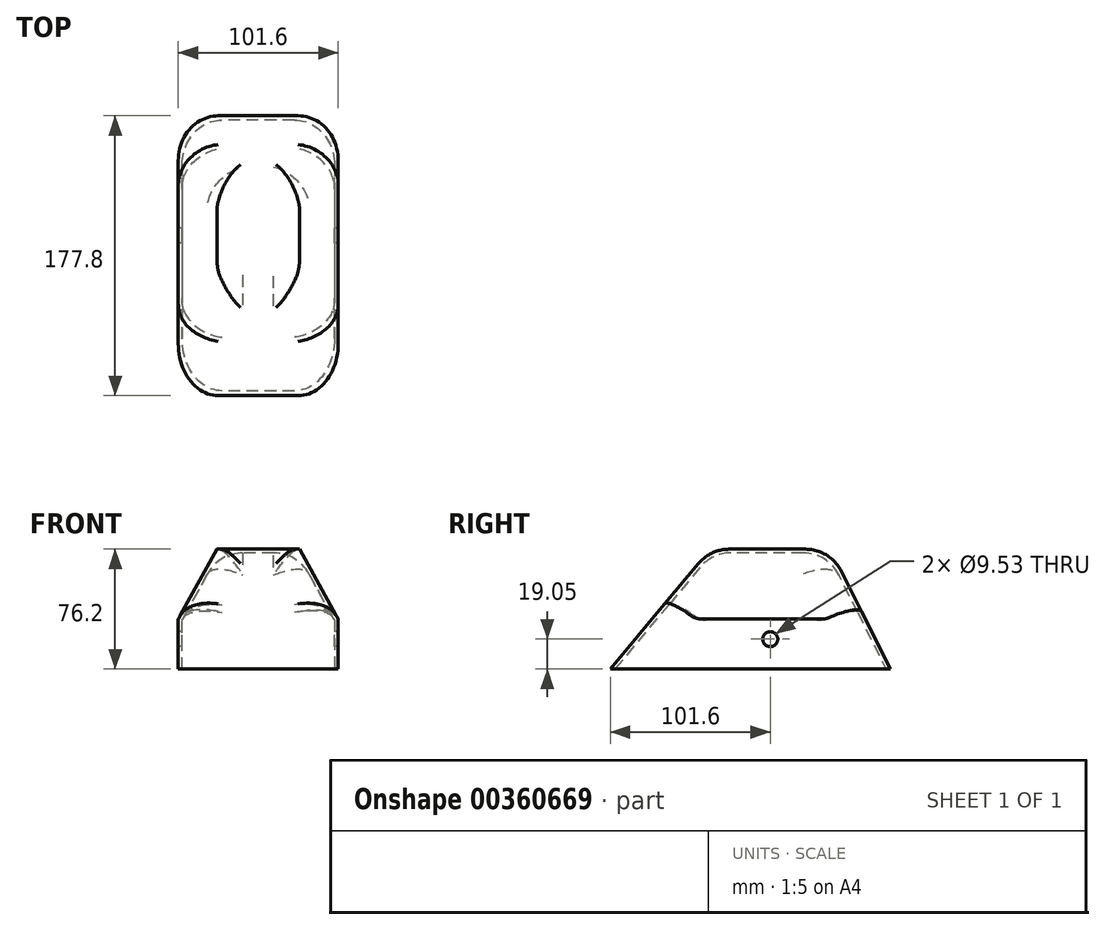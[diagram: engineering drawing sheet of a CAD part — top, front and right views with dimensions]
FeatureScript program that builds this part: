
annotation { "Feature Type Name" : "Feature", "Feature Type Description" : "" }
export const myFeature = defineFeature(function(context is Context, id is Id, definition is map)
    precondition{}
    {
        {
            var Q0;
            Q0=qCreatedBy(makeId("Right.planeOp"),FACE);
            var sketch = newSketch(context, id + "F0", { "sketchPlane" : qUnion([Q0])});
            skLineSegment(sketch, "E0", {"start": v(0, 0) * mm, "end": v(-101.6, 0) * mm});
            skLineSegment(sketch, "E1", {"start": v(-101.6, 0) * mm, "end": v(-38.1, 76.2) * mm});
            skLineSegment(sketch, "E2", {"start": v(-38.1, 76.2) * mm, "end": v(38.1, 76.2) * mm});
            skLineSegment(sketch, "E3", {"start": v(38.1, 76.2) * mm, "end": v(76.2, 0) * mm});
            skLineSegment(sketch, "E4", {"start": v(76.2, 0) * mm, "end": v(0, 0) * mm});
            skLineSegment(sketch, "E5", {"start": v(-38.1, 76.2) * mm, "end": v(0, 0) * mm, "construction": true});
            skLineSegment(sketch, "E6", {"start": v(38.1, 76.2) * mm, "end": v(0, 0) * mm, "construction": true});
            skSolve(sketch);
        }
        {
            var Q0;
            {var subQ1=sQuery(id+"F0.wireOp",EDGE,"E1");Q0=makeQuery(id+"F0.imprint","IMPRINT",FACE,{"disambiguationData":[TD([[makeQuery(id+"F0.imprint","IMPRINT",EDGE,{"derivedFrom":subQ1}),-1.0]])]});}
            extrude(context, id + "F1", {"entities" : qUnion([Q0]), "depth" : 101.6 * mm});
        }
        {
            var Q0;
            Q0=qCreatedBy(makeId("Right.planeOp"),FACE);
            var sketch = newSketch(context, id + "F2", { "sketchPlane" : qUnion([Q0])});
            skCircle(sketch, "E7", {"center": v(0, 19.05) * mm, "radius": 4.76 * mm});
            skSolve(sketch);
        }
        {
            var Q0;
            Q0=qCreatedBy(makeId("Front.planeOp"),FACE);
            var sketch = newSketch(context, id + "F3", { "sketchPlane" : qUnion([Q0])});
            skLineSegment(sketch, "E8", {"start": v(0, 0) * mm, "end": v(0, 31.75) * mm});
            skLineSegment(sketch, "E9", {"start": v(0, 31.75) * mm, "end": v(24.6, 76.2) * mm});
            skLineSegment(sketch, "E10", {"start": v(24.6, 76.2) * mm, "end": v(77, 76.2) * mm});
            skLineSegment(sketch, "E11", {"start": v(77, 76.2) * mm, "end": v(101.6, 31.75) * mm});
            skLineSegment(sketch, "E12", {"start": v(101.6, 31.75) * mm, "end": v(145.44, 31.75) * mm});
            skLineSegment(sketch, "E13", {"start": v(145.44, 31.75) * mm, "end": v(145.44, 123.88) * mm});
            skLineSegment(sketch, "E14", {"start": v(145.44, 123.88) * mm, "end": v(-43.84, 123.88) * mm});
            skLineSegment(sketch, "E15", {"start": v(-43.84, 123.88) * mm, "end": v(-43.84, 31.75) * mm});
            skLineSegment(sketch, "E16", {"start": v(-43.84, 31.75) * mm, "end": v(0, 31.75) * mm});
            skSolve(sketch);
        }
        {
            var Q0;
            Q0=makeQuery(id+"F3.imprint","IMPRINT",FACE,{"disambiguationData":[TD([[makeQuery(id+"F3.imprint","IMPRINT",EDGE,{"derivedFrom":sQuery(id+"F3.wireOp",EDGE,"E9")}),1.0]])]});
            extrude(context, id + "F4", {"entities" : qUnion([Q0]), "operationType" : NewBodyOperationType.REMOVE, "endBound" : BoundingType.THROUGH_ALL, "oppositeDirection" : true, "depth" : 25.4 * mm, "hasSecondDirection" : true, "secondDirectionBound" : SecondDirectionBoundingType.THROUGH_ALL, "secondDirectionOppositeDirection" : false, "secondDirectionDepth" : 25.4 * mm});
        }
        {
            var Q0;
            Q0=makeQuery(id+"F1.opExtrude","SWEPT_FACE",FACE,{"disambiguationData":[OSD([sQuery(id+"F0.wireOp",EDGE,"E0"),sQuery(id+"F0.wireOp",EDGE,"E4")])]});
            shell(context, id + "F5", {"entities" : qUnion([Q0]), "thickness" : 2.38 * mm});
        }
        {
            var Q0;
            Q0=qSketchRegion(id+"F2",true);
            extrude(context, id + "F6", {"entities" : qUnion([Q0]), "operationType" : NewBodyOperationType.REMOVE, "endBound" : BoundingType.THROUGH_ALL, "depth" : 25.4 * mm});
        }
        {
            var Q0;
            {var subQ0=sQuery(id+"F0.wireOp",EDGE,"E3");Q0=makeQuery(id+"F5.opShell","OFFSET_EDGE",EDGE,{"disambiguationData":[OSD([subQ0]),TDD([makeQuery(id+"F1.opExtrude","CAP_EDGE",EDGE,{"disambiguationData":[OSD([subQ0])],"isStart":true})])]});}
            var Q1;
            Q1=makeQuery(id+"F5.opShell","OFFSET_EDGE",EDGE,{"disambiguationData":[OSD([sQuery(id+"F3.wireOp",EDGE,"E9"),sQuery(id+"F3.wireOp",EDGE,"E16")])]});
            var Q2;
            {var subQ0=sQuery(id+"F0.wireOp",EDGE,"E1");Q2=makeQuery(id+"F5.opShell","OFFSET_EDGE",EDGE,{"disambiguationData":[OSD([subQ0]),TDD([makeQuery(id+"F1.opExtrude","CAP_EDGE",EDGE,{"disambiguationData":[OSD([subQ0])],"isStart":true})])]});}
            var Q3;
            Q3=makeQuery(id+"F5.opShell","OFFSET_EDGE",EDGE,{"disambiguationData":[OSD([sQuery(id+"F3.wireOp",EDGE,"E9"),sQuery(id+"F3.wireOp",EDGE,"E10")])]});
            var Q4;
            Q4=makeQuery(id+"F5.opShell","OFFSET_EDGE",EDGE,{"disambiguationData":[OSD([sQuery(id+"F0.wireOp",EDGE,"E2"),sQuery(id+"F0.wireOp",EDGE,"E3")])]});
            var Q5;
            Q5=makeQuery(id+"F5.opShell","OFFSET_EDGE",EDGE,{"disambiguationData":[OSD([sQuery(id+"F0.wireOp",EDGE,"E1"),sQuery(id+"F0.wireOp",EDGE,"E2")])]});
            var Q6;
            Q6=makeQuery(id+"F5.opShell","OFFSET_EDGE",EDGE,{"disambiguationData":[OSD([sQuery(id+"F0.wireOp",EDGE,"E1"),sQuery(id+"F3.wireOp",EDGE,"E11")])]});
            var Q7;
            Q7=makeQuery(id+"F5.opShell","OFFSET_EDGE",EDGE,{"disambiguationData":[OSD([sQuery(id+"F0.wireOp",EDGE,"E3"),sQuery(id+"F3.wireOp",EDGE,"E11")])]});
            var Q8;
            Q8=makeQuery(id+"F5.opShell","OFFSET_EDGE",EDGE,{"disambiguationData":[OSD([sQuery(id+"F3.wireOp",EDGE,"E11"),sQuery(id+"F3.wireOp",EDGE,"E12")])]});
            var Q9;
            Q9=makeQuery(id+"F5.opShell","OFFSET_EDGE",EDGE,{"disambiguationData":[OSD([sQuery(id+"F0.wireOp",EDGE,"E1"),sQuery(id+"F3.wireOp",EDGE,"E9")])]});
            var Q10;
            {var subQ0=sQuery(id+"F0.wireOp",EDGE,"E1");Q10=makeQuery(id+"F5.opShell","OFFSET_EDGE",EDGE,{"disambiguationData":[OSD([subQ0]),TDD([makeQuery(id+"F1.opExtrude","CAP_EDGE",EDGE,{"disambiguationData":[OSD([subQ0])],"isStart":false})])]});}
            var Q11;
            {var subQ0=sQuery(id+"F0.wireOp",EDGE,"E3");Q11=makeQuery(id+"F5.opShell","OFFSET_EDGE",EDGE,{"disambiguationData":[OSD([subQ0]),TDD([makeQuery(id+"F1.opExtrude","CAP_EDGE",EDGE,{"disambiguationData":[OSD([subQ0])],"isStart":false})])]});}
            var Q12;
            Q12=makeQuery(id+"F5.opShell","OFFSET_EDGE",EDGE,{"disambiguationData":[OSD([sQuery(id+"F3.wireOp",EDGE,"E10"),sQuery(id+"F3.wireOp",EDGE,"E11")])]});
            var Q13;
            Q13=makeQuery(id+"F5.opShell","OFFSET_EDGE",EDGE,{"disambiguationData":[OSD([sQuery(id+"F0.wireOp",EDGE,"E3"),sQuery(id+"F3.wireOp",EDGE,"E9")])]});
            var Q14;
            Q14=makeQuery(id+"F1.opExtrude","CAP_EDGE",EDGE,{"disambiguationData":[OSD([sQuery(id+"F0.wireOp",EDGE,"E1")])],"isStart":true});
            var Q15;
            Q15=makeQuery(id+"F4.boolean.opBoolean","COPY",EDGE,{"derivedFrom":makeQuery(id+"F4.opExtrude","SWEPT_EDGE",EDGE,{"disambiguationData":[OSD([sQuery(id+"F3.wireOp",EDGE,"E9"),sQuery(id+"F3.wireOp",EDGE,"E16")])]})});
            var Q16;
            Q16=makeQuery(id+"F4.boolean.opBoolean","INTERSECT",EDGE,{"derivedFrom":[makeQuery(id+"F1.opExtrude","SWEPT_FACE",FACE,{"disambiguationData":[OSD([sQuery(id+"F0.wireOp",EDGE,"E1")])]}),makeQuery(id+"F4.opExtrude","SWEPT_FACE",FACE,{"disambiguationData":[OSD([sQuery(id+"F3.wireOp",EDGE,"E9")])]})]});
            var Q17;
            Q17=makeQuery(id+"F4.boolean.opBoolean","COPY",EDGE,{"derivedFrom":makeQuery(id+"F4.opExtrude","SWEPT_EDGE",EDGE,{"disambiguationData":[OSD([sQuery(id+"F3.wireOp",EDGE,"E9"),sQuery(id+"F3.wireOp",EDGE,"E10")])]})});
            var Q18;
            Q18=makeQuery(id+"F4.boolean.opBoolean","INTERSECT",EDGE,{"derivedFrom":[makeQuery(id+"F1.opExtrude","SWEPT_FACE",FACE,{"disambiguationData":[OSD([sQuery(id+"F0.wireOp",EDGE,"E3")])]}),makeQuery(id+"F4.opExtrude","SWEPT_FACE",FACE,{"disambiguationData":[OSD([sQuery(id+"F3.wireOp",EDGE,"E9")])]})]});
            var Q19;
            Q19=makeQuery(id+"F1.opExtrude","CAP_EDGE",EDGE,{"disambiguationData":[OSD([sQuery(id+"F0.wireOp",EDGE,"E3")])],"isStart":true});
            var Q20;
            Q20=makeQuery(id+"F1.opExtrude","SWEPT_EDGE",EDGE,{"disambiguationData":[OSD([sQuery(id+"F0.wireOp",EDGE,"E1"),sQuery(id+"F0.wireOp",EDGE,"E2")])]});
            var Q21;
            Q21=makeQuery(id+"F4.boolean.opBoolean","COPY",EDGE,{"derivedFrom":makeQuery(id+"F4.opExtrude","SWEPT_EDGE",EDGE,{"disambiguationData":[OSD([sQuery(id+"F3.wireOp",EDGE,"E10"),sQuery(id+"F3.wireOp",EDGE,"E11")])]})});
            var Q22;
            Q22=makeQuery(id+"F4.boolean.opBoolean","INTERSECT",EDGE,{"derivedFrom":[makeQuery(id+"F1.opExtrude","SWEPT_FACE",FACE,{"disambiguationData":[OSD([sQuery(id+"F0.wireOp",EDGE,"E1")])]}),makeQuery(id+"F4.opExtrude","SWEPT_FACE",FACE,{"disambiguationData":[OSD([sQuery(id+"F3.wireOp",EDGE,"E11")])]})]});
            var Q23;
            Q23=makeQuery(id+"F1.opExtrude","CAP_EDGE",EDGE,{"disambiguationData":[OSD([sQuery(id+"F0.wireOp",EDGE,"E1")])],"isStart":false});
            var Q24;
            Q24=makeQuery(id+"F4.boolean.opBoolean","COPY",EDGE,{"derivedFrom":makeQuery(id+"F4.opExtrude","SWEPT_EDGE",EDGE,{"disambiguationData":[OSD([sQuery(id+"F3.wireOp",EDGE,"E11"),sQuery(id+"F3.wireOp",EDGE,"E12")])]})});
            var Q25;
            Q25=makeQuery(id+"F1.opExtrude","CAP_EDGE",EDGE,{"disambiguationData":[OSD([sQuery(id+"F0.wireOp",EDGE,"E3")])],"isStart":false});
            var Q26;
            Q26=makeQuery(id+"F4.boolean.opBoolean","INTERSECT",EDGE,{"derivedFrom":[makeQuery(id+"F1.opExtrude","SWEPT_FACE",FACE,{"disambiguationData":[OSD([sQuery(id+"F0.wireOp",EDGE,"E3")])]}),makeQuery(id+"F4.opExtrude","SWEPT_FACE",FACE,{"disambiguationData":[OSD([sQuery(id+"F3.wireOp",EDGE,"E11")])]})]});
            var Q27;
            Q27=makeQuery(id+"F1.opExtrude","SWEPT_EDGE",EDGE,{"disambiguationData":[OSD([sQuery(id+"F0.wireOp",EDGE,"E2"),sQuery(id+"F0.wireOp",EDGE,"E3")])]});
            fillet(context, id + "F7", {"entities" : qUnion([Q0, Q1, Q2, Q3, Q4, Q5, Q6, Q7, Q8, Q9, Q10, Q11, Q12, Q13, Q14, Q15, Q16, Q17, Q18, Q19, Q20, Q21, Q22, Q23, Q24, Q25, Q26, Q27]), "radius" : 25.4 * mm, "tangentPropagation" : true, "allowEdgeOverflow" : false});
        }
    });
